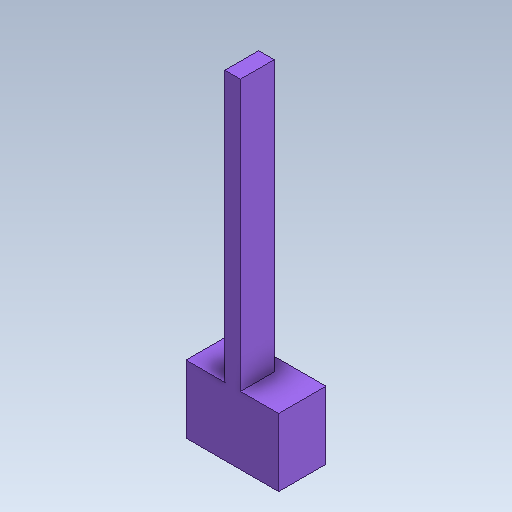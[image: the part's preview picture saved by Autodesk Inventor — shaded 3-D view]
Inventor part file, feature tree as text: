
AUTODESK INVENTOR PART (.ipt)
format: ipt  version: 2020 (Build 240168000, 168)  size: 123,392 bytes
history: native  units: in
note: dims shown in document units (in); Inventor stores cm internally (conversion verified against a paired STEP export)
features: sketch x13, other x3
ambient origin geometry x8: Origin, YZ Plane, XZ Plane, XY Plane, X Axis, Y Axis, Z Axis, Center Point
bodies: Solid1 (feature_tree)
feature tree (16):
  other  "PistonTop.ipt"
  other  "Solid1::PistonTop.ipt"
  other  "TaggingFeature1"
  sketch  "Sketch1"  dims[d0=0.3937in]
  sketch  "Sketch4"
  sketch  "Sketch5"
  sketch  "Sketch6"
  sketch  "Sketch7"
  sketch  "Sketch8"
  sketch  "Sketch9"
  sketch  "Sketch10"
  sketch  "Sketch11"
  sketch  "Sketch12"
  sketch  "Sketch17"
  sketch  "Sketch18"
  sketch  "Sketch19"
